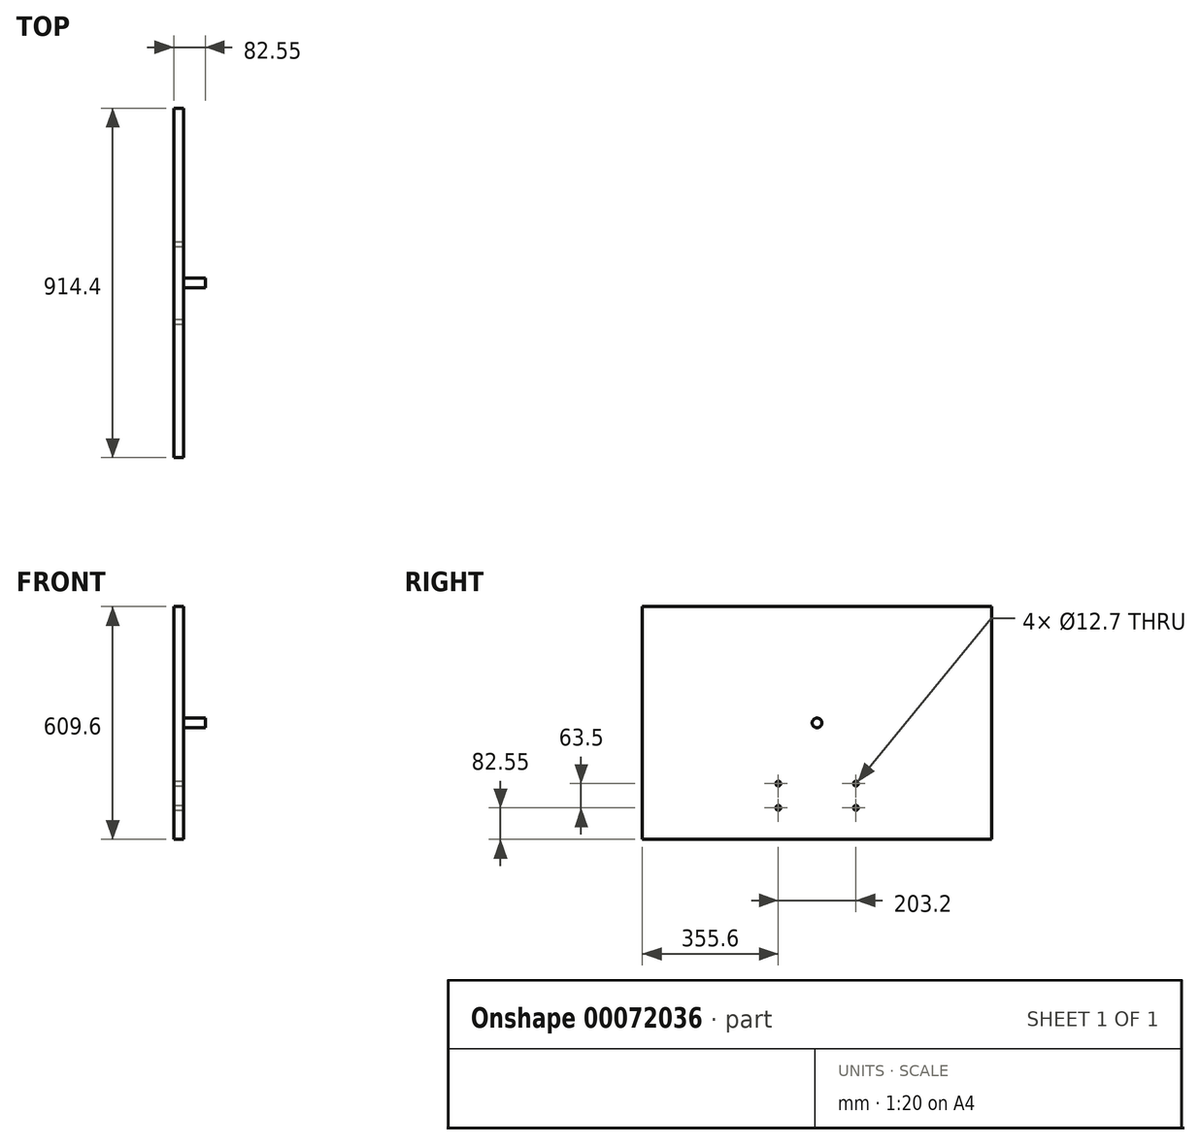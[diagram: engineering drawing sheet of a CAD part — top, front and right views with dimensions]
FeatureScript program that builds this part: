
annotation { "Feature Type Name" : "Feature", "Feature Type Description" : "" }
export const myFeature = defineFeature(function(context is Context, id is Id, definition is map)
    precondition{}
    {
        {
            var Q0;
            Q0=qCreatedBy(makeId("Right.planeOp"),FACE);
            var sketch = newSketch(context, id + "F0", { "sketchPlane" : qUnion([Q0])});
            skLineSegment(sketch, "E0.bottom", {"start": v(457.2, 304.8) * mm, "end": v(-457.2, 304.8) * mm});
            skLineSegment(sketch, "E0.top", {"start": v(457.2, -304.8) * mm, "end": v(-457.2, -304.8) * mm});
            skLineSegment(sketch, "E0.left", {"start": v(457.2, 304.8) * mm, "end": v(457.2, -304.8) * mm});
            skLineSegment(sketch, "E0.right", {"start": v(-457.2, 304.8) * mm, "end": v(-457.2, -304.8) * mm});
            skPoint(sketch, "E0.middle", {"position": v(0, 0) * mm});
            skSolve(sketch);
        }
        {
            var Q0;
            Q0 = qSketchRegion(id + "F0", true);
            extrude(context, id + "F1", {"entities" : qUnion([Q0]), "depth" : 25.4 * mm});
        }
        {
            var Q0;
            Q0=makeQuery(id+"F1.opExtrude","CAP_FACE",FACE,{"disambiguationData":[OSD([sQuery(id+"F0.wireOp",EDGE,"E0.bottom"),sQuery(id+"F0.wireOp",EDGE,"E0.top"),sQuery(id+"F0.wireOp",EDGE,"E0.left"),sQuery(id+"F0.wireOp",EDGE,"E0.right")])],"isStart":false});
            var sketch = newSketch(context, id + "F2", { "sketchPlane" : qUnion([Q0])});
            skCircle(sketch, "E1", {"center": v(0, 0) * mm, "radius": 12.7 * mm});
            skSolve(sketch);
        }
        {
            var Q0;
            Q0 = qSketchRegion(id + "F2", true);
            extrude(context, id + "F3", {"entities" : qUnion([Q0]), "operationType" : NewBodyOperationType.ADD, "depth" : 57.15 * mm});
        }
        {
            var Q0;
            Q0=makeQuery(id+"F1.opExtrude","CAP_FACE",FACE,{"disambiguationData":[OSD([sQuery(id+"F0.wireOp",EDGE,"E0.bottom"),sQuery(id+"F0.wireOp",EDGE,"E0.top"),sQuery(id+"F0.wireOp",EDGE,"E0.left"),sQuery(id+"F0.wireOp",EDGE,"E0.right")])],"isStart":false});
            var sketch = newSketch(context, id + "F4", { "sketchPlane" : qUnion([Q0])});
            skLineSegment(sketch, "E2.bottom", {"start": v(-101.6, -222.25) * mm, "end": v(101.6, -222.25) * mm});
            skLineSegment(sketch, "E2.top", {"start": v(-101.6, -158.75) * mm, "end": v(101.6, -158.75) * mm});
            skLineSegment(sketch, "E2.left", {"start": v(-101.6, -222.25) * mm, "end": v(-101.6, -158.75) * mm});
            skLineSegment(sketch, "E2.right", {"start": v(101.6, -222.25) * mm, "end": v(101.6, -158.75) * mm});
            skSolve(sketch);
        }
        {
            var Q0;
            Q0=sQuery(id+"F4.wireOp",VERTEX,"E2.left.end");
            var Q1;
            Q1=sQuery(id+"F4.wireOp",VERTEX,"E2.top.end");
            var Q2;
            Q2=sQuery(id+"F4.wireOp",VERTEX,"E2.right.start");
            var Q3;
            Q3=sQuery(id+"F4.wireOp",VERTEX,"E2.left.start");
            var Q4;
            Q4=makeQuery(id+"F1.opExtrude","SWEPT_BODY",BODY,{"disambiguationData":[OSD([sQuery(id+"F0.wireOp",EDGE,"E0.bottom"),sQuery(id+"F0.wireOp",EDGE,"E0.top"),sQuery(id+"F0.wireOp",EDGE,"E0.left"),sQuery(id+"F0.wireOp",EDGE,"E0.right")])]});
            hole(context, id + "F5", {"style" : HoleStyle.SIMPLE, "holeDiameter" : 12.7 * mm, "endStyle" : HoleEndStyle.THROUGH, "locations" : qUnion([Q0, Q1, Q2, Q3]), "scope" : qUnion([Q4])});
        }
    });
